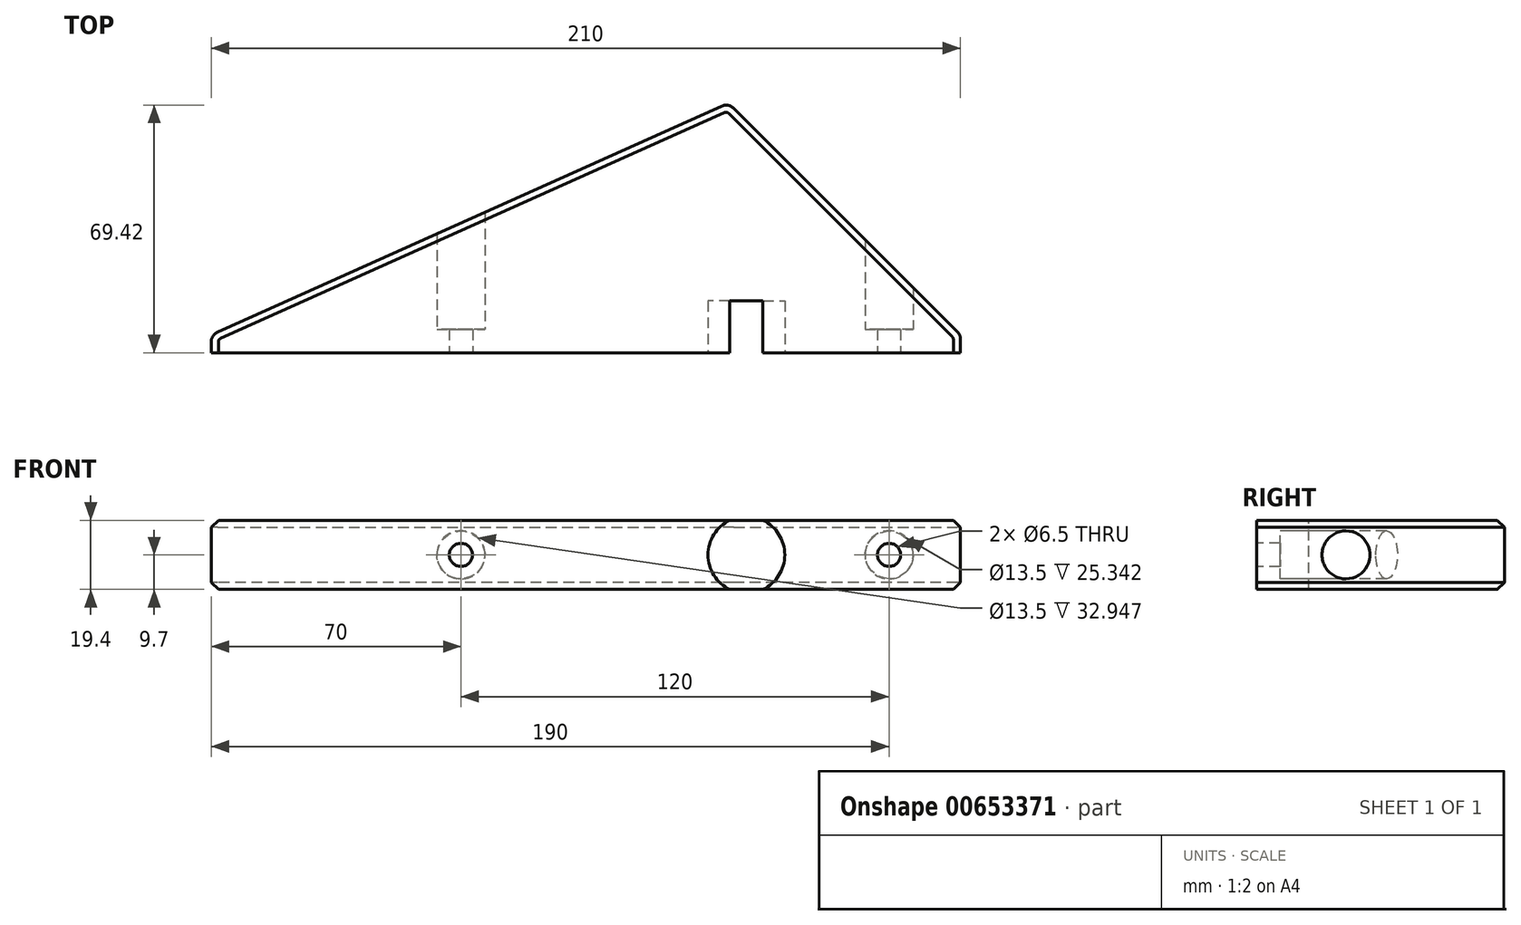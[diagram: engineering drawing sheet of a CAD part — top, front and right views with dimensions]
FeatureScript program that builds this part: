
annotation { "Feature Type Name" : "Feature", "Feature Type Description" : "" }
export const myFeature = defineFeature(function(context is Context, id is Id, definition is map)
    precondition{}
    {
        {
            var Q0;
            Q0=qCreatedBy(makeId("Top.planeOp"),FACE);
            var sketch = newSketch(context, id + "F0", { "sketchPlane" : qUnion([Q0])});
            skLineSegment(sketch, "E0.top", {"start": v(-105, -44.95) * mm, "end": v(105, -44.95) * mm});
            skLineSegment(sketch, "E0.left", {"start": v(-105, -39.95) * mm, "end": v(-105, -44.95) * mm});
            skLineSegment(sketch, "E0.right", {"start": v(105, -39.95) * mm, "end": v(105, -44.95) * mm});
            skLineSegment(sketch, "E1", {"start": v(-105, -39.95) * mm, "end": v(40, 25.05) * mm});
            skLineSegment(sketch, "E2", {"start": v(40, 25.05) * mm, "end": v(105, -39.95) * mm});
            skSolve(sketch);
        }
        {
            var Q0;
            Q0=makeQuery(id+"F0.imprint","IMPRINT",FACE,{"disambiguationData":[TD([[makeQuery(id+"F0.imprint","IMPRINT",EDGE,{"derivedFrom":sQuery(id+"F0.wireOp",EDGE,"E0.top")}),1.0]])]});
            extrude(context, id + "F1", {"entities" : qUnion([Q0]), "depth" : 19.4 * mm, "offsetDistance" : 25 * mm});
        }
        {
            var Q0;
            Q0=makeQuery(id+"F1.opExtrude","SWEPT_EDGE",EDGE,{"disambiguationData":[OSD([sQuery(id+"F0.wireOp",EDGE,"E1"),sQuery(id+"F0.wireOp",EDGE,"E2")])]});
            var Q1;
            Q1=makeQuery(id+"F1.opExtrude","SWEPT_EDGE",EDGE,{"disambiguationData":[OSD([sQuery(id+"F0.wireOp",EDGE,"E0.right"),sQuery(id+"F0.wireOp",EDGE,"E2")])]});
            var Q2;
            Q2=makeQuery(id+"F1.opExtrude","SWEPT_EDGE",EDGE,{"disambiguationData":[OSD([sQuery(id+"F0.wireOp",EDGE,"E0.left"),sQuery(id+"F0.wireOp",EDGE,"E1")])]});
            fillet(context, id + "F2", {"entities" : qUnion([Q0, Q1, Q2]), "radius" : 3 * mm, "tangentPropagation" : true, "allowEdgeOverflow" : false});
        }
        {
            var Q0;
            Q0=makeQuery(id+"F1.opExtrude","SWEPT_FACE",FACE,{"disambiguationData":[OSD([sQuery(id+"F0.wireOp",EDGE,"E0.top")])]});
            var sketch = newSketch(context, id + "F3", { "sketchPlane" : qUnion([Q0])});
            skCircle(sketch, "E3", {"center": v(45, 9.7) * mm, "radius": 10.75 * mm});
            skSolve(sketch);
        }
        {
            var Q0;
            {var subQ0=sQuery(id+"F3.wireOp",EDGE,"E3");var subQ1=sQuery(id+"F0.wireOp",EDGE,"E0.top");var subQ2=makeQuery(id+"F1.opExtrude","CAP_EDGE",EDGE,{"disambiguationData":[OSD([subQ1])],"isStart":false});var subQ3=makeQuery(id+"F3.imprint","INTERSECT",VERTEX,{"disambiguationData":[OD(0.0)],"derivedFrom":[subQ2,subQ0]});Q0=makeQuery(id+"F3.imprint","IMPRINT",FACE,{"disambiguationData":[TD([[makeQuery(id+"F3.imprint","IMPRINT",EDGE,{"disambiguationData":[TD([[subQ3,-1.0]])],"derivedFrom":subQ0}),1.0]])]});}
            extrude(context, id + "F4", {"entities" : qUnion([Q0]), "operationType" : NewBodyOperationType.REMOVE, "oppositeDirection" : true, "depth" : 14.5 * mm, "offsetDistance" : 25 * mm});
        }
        {
            var Q0;
            {var subQ3=sQuery(id+"F0.wireOp",EDGE,"E0.left");var subQ4=sQuery(id+"F0.wireOp",EDGE,"E0.top");Q0=makeQuery(id+"F4.boolean.opBoolean","SPLIT",FACE,{"disambiguationData":[TD([makeQuery(id+"F1.opExtrude","SWEPT_FACE",FACE,{"disambiguationData":[OSD([subQ3])]})])],"derivedFrom":makeQuery(id+"F1.opExtrude","SWEPT_FACE",FACE,{"disambiguationData":[OSD([subQ4])]})});}
            var sketch = newSketch(context, id + "F5", { "sketchPlane" : qUnion([Q0])});
            skLineSegment(sketch, "E4", {"start": v(-121.45, 9.7) * mm, "end": v(291.45, 9.7) * mm, "construction": true});
            skCircle(sketch, "E5", {"center": v(-35, 9.7) * mm, "radius": 3.25 * mm});
            skCircle(sketch, "E6", {"center": v(85, 9.7) * mm, "radius": 3.25 * mm});
            skSolve(sketch);
        }
        {
            var Q0;
            Q0=makeQuery(id+"F5.imprint","IMPRINT",FACE,{"disambiguationData":[TD([[makeQuery(id+"F5.imprint","IMPRINT",EDGE,{"derivedFrom":sQuery(id+"F5.wireOp",EDGE,"E5")}),1.0]])]});
            var Q1;
            Q1=makeQuery(id+"F5.imprint","IMPRINT",FACE,{"disambiguationData":[TD([[makeQuery(id+"F5.imprint","IMPRINT",EDGE,{"derivedFrom":sQuery(id+"F5.wireOp",EDGE,"E6")}),1.0]])]});
            extrude(context, id + "F6", {"entities" : qUnion([Q0, Q1]), "operationType" : NewBodyOperationType.REMOVE, "endBound" : BoundingType.THROUGH_ALL, "oppositeDirection" : true, "depth" : 25 * mm, "offsetDistance" : 25 * mm});
        }
        {
            var Q0;
            Q0=qCreatedBy(makeId("Front.planeOp"),FACE);
            var Q1;
            {var subQ0=sQuery(id+"F3.wireOp",EDGE,"E3");var subQ1=sQuery(id+"F0.wireOp",EDGE,"E0.top");Q1=makeQuery(id+"F4.boolean.opBoolean","COPY",VERTEX,{"derivedFrom":makeQuery(id+"F4.opExtrude","CAP_VERTEX",VERTEX,{"disambiguationData":[OSD([subQ1,subQ0]),TDD([makeQuery(id+"F3.imprint","INTERSECT",VERTEX,{"disambiguationData":[OD(1.0)],"derivedFrom":[makeQuery(id+"F1.opExtrude","CAP_EDGE",EDGE,{"disambiguationData":[OSD([subQ1])],"isStart":true}),subQ0]})])],"isStart":true})});}
            cPlane(context, id + "F7", {"entities" : qUnion([Q0, Q1]), "cplaneType" : CPlaneType.PLANE_POINT, "offset" : 25 * mm, "width" : 150 * mm, "height" : 150 * mm});
        }
        {
            var Q0;
            Q0=qCreatedBy(id+"F7.planeOp",FACE);
            cPlane(context, id + "F8", {"entities" : qUnion([Q0]), "cplaneType" : CPlaneType.OFFSET, "offset" : 6.5 * mm, "oppositeDirection" : true, "width" : 150 * mm, "height" : 150 * mm});
        }
        {
            var Q0;
            Q0=qCreatedBy(id+"F8.planeOp",FACE);
            var sketch = newSketch(context, id + "F9", { "sketchPlane" : qUnion([Q0])});
            skCircle(sketch, "E7", {"center": v(85, 9.7) * mm, "radius": 6.75 * mm});
            skCircle(sketch, "E8", {"center": v(-35, 9.7) * mm, "radius": 6.75 * mm});
            skSolve(sketch);
        }
        {
            var Q0;
            Q0 = qSketchRegion(id + "F9", true);
            extrude(context, id + "F10", {"entities" : qUnion([Q0]), "operationType" : NewBodyOperationType.REMOVE, "endBound" : BoundingType.THROUGH_ALL, "oppositeDirection" : true, "depth" : 25 * mm, "offsetDistance" : 25 * mm});
        }
        {
            var Q0;
            Q0=makeQuery(id+"F1.opExtrude","CAP_EDGE",EDGE,{"disambiguationData":[OSD([sQuery(id+"F0.wireOp",EDGE,"E0.left")])],"isStart":false});
            var Q1;
            {var subQ0=sQuery(id+"F0.wireOp",EDGE,"E1");var subQ1=sQuery(id+"F0.wireOp",EDGE,"E0.left");Q1=makeQuery(id+"F2.opFillet","BLEND_EDGE",EDGE,{"blendedFrom":[makeQuery(id+"F1.opExtrude","SWEPT_EDGE",EDGE,{"disambiguationData":[OSD([subQ1,subQ0])]}),makeQuery(id+"F1.opExtrude","CAP_FACE",FACE,{"disambiguationData":[OSD([sQuery(id+"F0.wireOp",EDGE,"E0.top"),subQ1,sQuery(id+"F0.wireOp",EDGE,"E0.right"),subQ0,sQuery(id+"F0.wireOp",EDGE,"E2")])],"isStart":false})],"blendedInto":[makeQuery(id+"F1.opExtrude","CAP_FACE",FACE,{"disambiguationData":[OSD([sQuery(id+"F0.wireOp",EDGE,"E0.top"),subQ1,sQuery(id+"F0.wireOp",EDGE,"E0.right"),subQ0,sQuery(id+"F0.wireOp",EDGE,"E2")])],"isStart":false})]});}
            var Q2;
            Q2=makeQuery(id+"F1.opExtrude","CAP_EDGE",EDGE,{"disambiguationData":[OSD([sQuery(id+"F0.wireOp",EDGE,"E1")])],"isStart":false});
            var Q3;
            {var subQ0=sQuery(id+"F0.wireOp",EDGE,"E2");var subQ1=sQuery(id+"F0.wireOp",EDGE,"E1");Q3=makeQuery(id+"F2.opFillet","BLEND_EDGE",EDGE,{"blendedFrom":[makeQuery(id+"F1.opExtrude","SWEPT_EDGE",EDGE,{"disambiguationData":[OSD([subQ1,subQ0])]}),makeQuery(id+"F1.opExtrude","CAP_FACE",FACE,{"disambiguationData":[OSD([sQuery(id+"F0.wireOp",EDGE,"E0.top"),sQuery(id+"F0.wireOp",EDGE,"E0.left"),sQuery(id+"F0.wireOp",EDGE,"E0.right"),subQ1,subQ0])],"isStart":false})],"blendedInto":[makeQuery(id+"F1.opExtrude","CAP_FACE",FACE,{"disambiguationData":[OSD([sQuery(id+"F0.wireOp",EDGE,"E0.top"),sQuery(id+"F0.wireOp",EDGE,"E0.left"),sQuery(id+"F0.wireOp",EDGE,"E0.right"),subQ1,subQ0])],"isStart":false})]});}
            var Q4;
            Q4=makeQuery(id+"F1.opExtrude","CAP_EDGE",EDGE,{"disambiguationData":[OSD([sQuery(id+"F0.wireOp",EDGE,"E2")])],"isStart":false});
            var Q5;
            Q5=makeQuery(id+"F1.opExtrude","CAP_EDGE",EDGE,{"disambiguationData":[OSD([sQuery(id+"F0.wireOp",EDGE,"E0.right")])],"isStart":false});
            var Q6;
            Q6=makeQuery(id+"F1.opExtrude","CAP_EDGE",EDGE,{"disambiguationData":[OSD([sQuery(id+"F0.wireOp",EDGE,"E2")])],"isStart":true});
            chamfer(context, id + "F11", {"entities" : qUnion([Q0, Q1, Q2, Q3, Q4, Q5, Q6]), "width" : 2 * mm, "tangentPropagation" : true});
        }
    });
